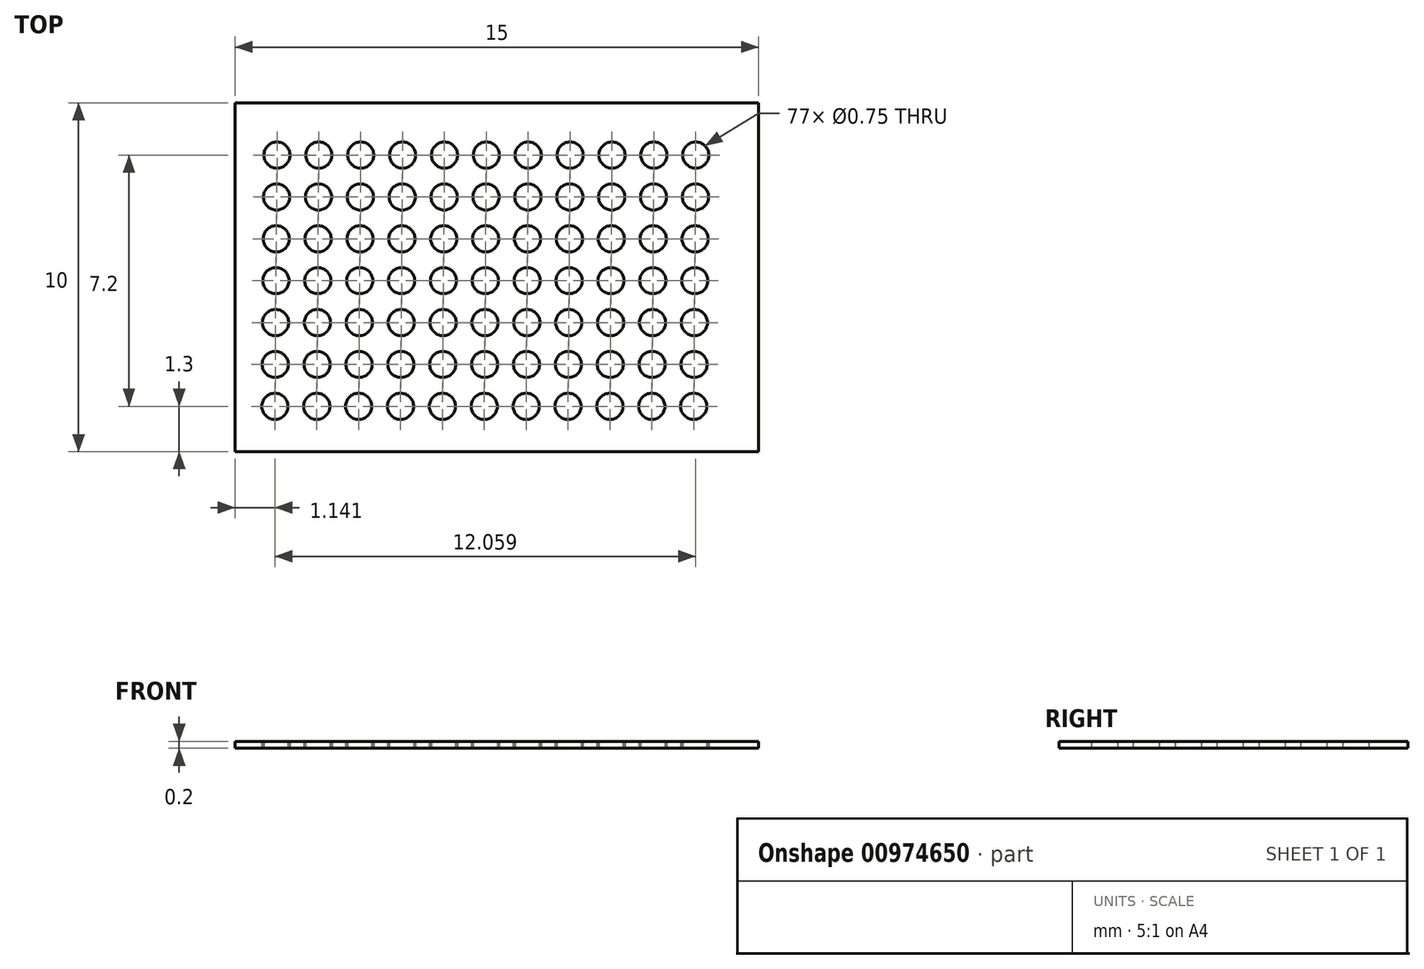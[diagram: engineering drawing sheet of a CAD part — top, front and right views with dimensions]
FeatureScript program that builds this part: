
annotation { "Feature Type Name" : "Feature", "Feature Type Description" : "" }
export const myFeature = defineFeature(function(context is Context, id is Id, definition is map)
    precondition{}
    {
        {
            var Q0;
            Q0=qCreatedBy(makeId("Top.planeOp"),FACE);
            var sketch = newSketch(context, id + "F0", { "sketchPlane" : qUnion([Q0])});
            skLineSegment(sketch, "E0.bottom", {"start": v(0, 0) * mm, "end": v(15, 0) * mm});
            skLineSegment(sketch, "E0.top", {"start": v(0, -10) * mm, "end": v(15, -10) * mm});
            skLineSegment(sketch, "E0.left", {"start": v(0, 0) * mm, "end": v(0, -10) * mm});
            skLineSegment(sketch, "E0.right", {"start": v(15, 0) * mm, "end": v(15, -10) * mm});
            skEllipse(sketch, "E1", {"center": v(1.2, -1.5) * mm, "majorRadius": 0.38 * mm, "minorRadius": 0.38 * mm, "majorAxis": v(0.93, 0.38)});
            skLineSegment(sketch, "E2.direction1", {"start": v(1.2, -1.5) * mm, "end": v(2.4, -1.5) * mm, "construction": true});
            skLineSegment(sketch, "E3.direction1", {"start": v(1.2, -1.2) * mm, "end": v(1.2, -2.1) * mm, "construction": true});
            skEllipse(sketch, "E4.0.1.0", {"center": v(2.4, -1.5) * mm, "majorRadius": 0.38 * mm, "minorRadius": 0.38 * mm, "majorAxis": v(0.93, 0.38)});
            skEllipse(sketch, "E4.0.2.0", {"center": v(3.6, -1.5) * mm, "majorRadius": 0.38 * mm, "minorRadius": 0.38 * mm, "majorAxis": v(0.93, 0.38)});
            skEllipse(sketch, "E4.0.3.0", {"center": v(4.8, -1.5) * mm, "majorRadius": 0.38 * mm, "minorRadius": 0.38 * mm, "majorAxis": v(0.93, 0.38)});
            skEllipse(sketch, "E4.0.4.0", {"center": v(6, -1.5) * mm, "majorRadius": 0.38 * mm, "minorRadius": 0.38 * mm, "majorAxis": v(0.93, 0.38)});
            skEllipse(sketch, "E4.0.5.0", {"center": v(7.2, -1.5) * mm, "majorRadius": 0.38 * mm, "minorRadius": 0.38 * mm, "majorAxis": v(0.93, 0.38)});
            skEllipse(sketch, "E4.0.6.0", {"center": v(8.4, -1.5) * mm, "majorRadius": 0.38 * mm, "minorRadius": 0.38 * mm, "majorAxis": v(0.93, 0.38)});
            skEllipse(sketch, "E4.0.7.0", {"center": v(9.6, -1.5) * mm, "majorRadius": 0.38 * mm, "minorRadius": 0.38 * mm, "majorAxis": v(0.93, 0.38)});
            skEllipse(sketch, "E4.0.8.0", {"center": v(10.8, -1.5) * mm, "majorRadius": 0.38 * mm, "minorRadius": 0.38 * mm, "majorAxis": v(0.93, 0.38)});
            skEllipse(sketch, "E4.0.9.0", {"center": v(12, -1.5) * mm, "majorRadius": 0.38 * mm, "minorRadius": 0.38 * mm, "majorAxis": v(0.93, 0.38)});
            skEllipse(sketch, "E4.0.10.0", {"center": v(13.2, -1.5) * mm, "majorRadius": 0.38 * mm, "minorRadius": 0.38 * mm, "majorAxis": v(0.93, 0.38)});
            skEllipse(sketch, "E5.1.0.0", {"center": v(2.4, -2.7) * mm, "majorRadius": 0.38 * mm, "minorRadius": 0.38 * mm, "majorAxis": v(0.93, 0.38)});
            skEllipse(sketch, "E5.1.0.1", {"center": v(1.2, -2.7) * mm, "majorRadius": 0.38 * mm, "minorRadius": 0.38 * mm, "majorAxis": v(0.93, 0.38)});
            skEllipse(sketch, "E5.1.0.2", {"center": v(6, -2.7) * mm, "majorRadius": 0.38 * mm, "minorRadius": 0.38 * mm, "majorAxis": v(0.93, 0.38)});
            skLineSegment(sketch, "E5.1.0.3", {"start": v(1.2, -2.7) * mm, "end": v(2.4, -2.7) * mm, "construction": true});
            skEllipse(sketch, "E5.1.0.4", {"center": v(3.6, -2.7) * mm, "majorRadius": 0.38 * mm, "minorRadius": 0.38 * mm, "majorAxis": v(0.93, 0.38)});
            skEllipse(sketch, "E5.1.0.5", {"center": v(8.4, -2.7) * mm, "majorRadius": 0.38 * mm, "minorRadius": 0.38 * mm, "majorAxis": v(0.93, 0.38)});
            skEllipse(sketch, "E5.1.0.6", {"center": v(9.6, -2.7) * mm, "majorRadius": 0.38 * mm, "minorRadius": 0.38 * mm, "majorAxis": v(0.93, 0.38)});
            skEllipse(sketch, "E5.1.0.7", {"center": v(7.2, -2.7) * mm, "majorRadius": 0.38 * mm, "minorRadius": 0.38 * mm, "majorAxis": v(0.93, 0.38)});
            skEllipse(sketch, "E5.1.0.8", {"center": v(13.2, -2.7) * mm, "majorRadius": 0.38 * mm, "minorRadius": 0.38 * mm, "majorAxis": v(0.93, 0.38)});
            skEllipse(sketch, "E5.1.0.9", {"center": v(4.8, -2.7) * mm, "majorRadius": 0.38 * mm, "minorRadius": 0.38 * mm, "majorAxis": v(0.93, 0.38)});
            skEllipse(sketch, "E5.1.0.10", {"center": v(12, -2.7) * mm, "majorRadius": 0.38 * mm, "minorRadius": 0.38 * mm, "majorAxis": v(0.93, 0.38)});
            skEllipse(sketch, "E5.1.0.11", {"center": v(10.8, -2.7) * mm, "majorRadius": 0.38 * mm, "minorRadius": 0.38 * mm, "majorAxis": v(0.93, 0.38)});
            skLineSegment(sketch, "E5.1.0.12", {"start": v(1.2, -2.4) * mm, "end": v(1.2, -3.3) * mm, "construction": true});
            skEllipse(sketch, "E5.2.0.0", {"center": v(2.38, -3.9) * mm, "majorRadius": 0.38 * mm, "minorRadius": 0.38 * mm, "majorAxis": v(0.93, 0.38)});
            skEllipse(sketch, "E5.2.0.1", {"center": v(1.18, -3.9) * mm, "majorRadius": 0.38 * mm, "minorRadius": 0.38 * mm, "majorAxis": v(0.93, 0.38)});
            skEllipse(sketch, "E5.2.0.2", {"center": v(5.98, -3.9) * mm, "majorRadius": 0.38 * mm, "minorRadius": 0.38 * mm, "majorAxis": v(0.93, 0.38)});
            skLineSegment(sketch, "E5.2.0.3", {"start": v(1.18, -3.9) * mm, "end": v(2.38, -3.9) * mm, "construction": true});
            skEllipse(sketch, "E5.2.0.4", {"center": v(3.58, -3.9) * mm, "majorRadius": 0.38 * mm, "minorRadius": 0.38 * mm, "majorAxis": v(0.93, 0.38)});
            skEllipse(sketch, "E5.2.0.5", {"center": v(8.38, -3.9) * mm, "majorRadius": 0.38 * mm, "minorRadius": 0.38 * mm, "majorAxis": v(0.93, 0.38)});
            skEllipse(sketch, "E5.2.0.6", {"center": v(9.58, -3.9) * mm, "majorRadius": 0.38 * mm, "minorRadius": 0.38 * mm, "majorAxis": v(0.93, 0.38)});
            skEllipse(sketch, "E5.2.0.7", {"center": v(7.18, -3.9) * mm, "majorRadius": 0.38 * mm, "minorRadius": 0.38 * mm, "majorAxis": v(0.93, 0.38)});
            skEllipse(sketch, "E5.2.0.8", {"center": v(13.18, -3.9) * mm, "majorRadius": 0.38 * mm, "minorRadius": 0.38 * mm, "majorAxis": v(0.93, 0.38)});
            skEllipse(sketch, "E5.2.0.9", {"center": v(4.78, -3.9) * mm, "majorRadius": 0.38 * mm, "minorRadius": 0.38 * mm, "majorAxis": v(0.93, 0.38)});
            skEllipse(sketch, "E5.2.0.10", {"center": v(11.98, -3.9) * mm, "majorRadius": 0.38 * mm, "minorRadius": 0.38 * mm, "majorAxis": v(0.93, 0.38)});
            skEllipse(sketch, "E5.2.0.11", {"center": v(10.78, -3.9) * mm, "majorRadius": 0.38 * mm, "minorRadius": 0.38 * mm, "majorAxis": v(0.93, 0.38)});
            skLineSegment(sketch, "E5.2.0.12", {"start": v(1.18, -3.6) * mm, "end": v(1.18, -4.5) * mm, "construction": true});
            skEllipse(sketch, "E5.3.0.0", {"center": v(2.37, -5.1) * mm, "majorRadius": 0.38 * mm, "minorRadius": 0.38 * mm, "majorAxis": v(0.93, 0.38)});
            skEllipse(sketch, "E5.3.0.1", {"center": v(1.17, -5.1) * mm, "majorRadius": 0.38 * mm, "minorRadius": 0.38 * mm, "majorAxis": v(0.93, 0.38)});
            skEllipse(sketch, "E5.3.0.2", {"center": v(5.97, -5.1) * mm, "majorRadius": 0.38 * mm, "minorRadius": 0.38 * mm, "majorAxis": v(0.93, 0.38)});
            skLineSegment(sketch, "E5.3.0.3", {"start": v(1.17, -5.1) * mm, "end": v(2.37, -5.1) * mm, "construction": true});
            skEllipse(sketch, "E5.3.0.4", {"center": v(3.57, -5.1) * mm, "majorRadius": 0.38 * mm, "minorRadius": 0.38 * mm, "majorAxis": v(0.93, 0.38)});
            skEllipse(sketch, "E5.3.0.5", {"center": v(8.37, -5.1) * mm, "majorRadius": 0.38 * mm, "minorRadius": 0.38 * mm, "majorAxis": v(0.93, 0.38)});
            skEllipse(sketch, "E5.3.0.6", {"center": v(9.57, -5.1) * mm, "majorRadius": 0.38 * mm, "minorRadius": 0.38 * mm, "majorAxis": v(0.93, 0.38)});
            skEllipse(sketch, "E5.3.0.7", {"center": v(7.17, -5.1) * mm, "majorRadius": 0.38 * mm, "minorRadius": 0.38 * mm, "majorAxis": v(0.93, 0.38)});
            skEllipse(sketch, "E5.3.0.8", {"center": v(13.17, -5.1) * mm, "majorRadius": 0.38 * mm, "minorRadius": 0.38 * mm, "majorAxis": v(0.93, 0.38)});
            skEllipse(sketch, "E5.3.0.9", {"center": v(4.77, -5.1) * mm, "majorRadius": 0.38 * mm, "minorRadius": 0.38 * mm, "majorAxis": v(0.93, 0.38)});
            skEllipse(sketch, "E5.3.0.10", {"center": v(11.97, -5.1) * mm, "majorRadius": 0.38 * mm, "minorRadius": 0.38 * mm, "majorAxis": v(0.93, 0.38)});
            skEllipse(sketch, "E5.3.0.11", {"center": v(10.77, -5.1) * mm, "majorRadius": 0.38 * mm, "minorRadius": 0.38 * mm, "majorAxis": v(0.93, 0.38)});
            skLineSegment(sketch, "E5.3.0.12", {"start": v(1.17, -4.8) * mm, "end": v(1.17, -5.7) * mm, "construction": true});
            skEllipse(sketch, "E5.4.0.0", {"center": v(2.36, -6.3) * mm, "majorRadius": 0.38 * mm, "minorRadius": 0.38 * mm, "majorAxis": v(0.93, 0.38)});
            skEllipse(sketch, "E5.4.0.1", {"center": v(1.16, -6.3) * mm, "majorRadius": 0.38 * mm, "minorRadius": 0.38 * mm, "majorAxis": v(0.93, 0.38)});
            skEllipse(sketch, "E5.4.0.2", {"center": v(5.96, -6.3) * mm, "majorRadius": 0.38 * mm, "minorRadius": 0.38 * mm, "majorAxis": v(0.93, 0.38)});
            skLineSegment(sketch, "E5.4.0.3", {"start": v(1.16, -6.3) * mm, "end": v(2.36, -6.3) * mm, "construction": true});
            skEllipse(sketch, "E5.4.0.4", {"center": v(3.56, -6.3) * mm, "majorRadius": 0.38 * mm, "minorRadius": 0.38 * mm, "majorAxis": v(0.93, 0.38)});
            skEllipse(sketch, "E5.4.0.5", {"center": v(8.36, -6.3) * mm, "majorRadius": 0.38 * mm, "minorRadius": 0.38 * mm, "majorAxis": v(0.93, 0.38)});
            skEllipse(sketch, "E5.4.0.6", {"center": v(9.56, -6.3) * mm, "majorRadius": 0.38 * mm, "minorRadius": 0.38 * mm, "majorAxis": v(0.93, 0.38)});
            skEllipse(sketch, "E5.4.0.7", {"center": v(7.16, -6.3) * mm, "majorRadius": 0.38 * mm, "minorRadius": 0.38 * mm, "majorAxis": v(0.93, 0.38)});
            skEllipse(sketch, "E5.4.0.8", {"center": v(13.16, -6.3) * mm, "majorRadius": 0.38 * mm, "minorRadius": 0.38 * mm, "majorAxis": v(0.93, 0.38)});
            skEllipse(sketch, "E5.4.0.9", {"center": v(4.76, -6.3) * mm, "majorRadius": 0.38 * mm, "minorRadius": 0.38 * mm, "majorAxis": v(0.93, 0.38)});
            skEllipse(sketch, "E5.4.0.10", {"center": v(11.96, -6.3) * mm, "majorRadius": 0.38 * mm, "minorRadius": 0.38 * mm, "majorAxis": v(0.93, 0.38)});
            skEllipse(sketch, "E5.4.0.11", {"center": v(10.76, -6.3) * mm, "majorRadius": 0.38 * mm, "minorRadius": 0.38 * mm, "majorAxis": v(0.93, 0.38)});
            skLineSegment(sketch, "E5.4.0.12", {"start": v(1.16, -6) * mm, "end": v(1.16, -6.9) * mm, "construction": true});
            skEllipse(sketch, "E5.5.0.0", {"center": v(2.35, -7.5) * mm, "majorRadius": 0.38 * mm, "minorRadius": 0.38 * mm, "majorAxis": v(0.93, 0.38)});
            skEllipse(sketch, "E5.5.0.1", {"center": v(1.15, -7.5) * mm, "majorRadius": 0.38 * mm, "minorRadius": 0.38 * mm, "majorAxis": v(0.93, 0.38)});
            skEllipse(sketch, "E5.5.0.2", {"center": v(5.95, -7.5) * mm, "majorRadius": 0.38 * mm, "minorRadius": 0.38 * mm, "majorAxis": v(0.93, 0.38)});
            skLineSegment(sketch, "E5.5.0.3", {"start": v(1.15, -7.5) * mm, "end": v(2.35, -7.5) * mm, "construction": true});
            skEllipse(sketch, "E5.5.0.4", {"center": v(3.55, -7.5) * mm, "majorRadius": 0.38 * mm, "minorRadius": 0.38 * mm, "majorAxis": v(0.93, 0.38)});
            skEllipse(sketch, "E5.5.0.5", {"center": v(8.35, -7.5) * mm, "majorRadius": 0.38 * mm, "minorRadius": 0.38 * mm, "majorAxis": v(0.93, 0.38)});
            skEllipse(sketch, "E5.5.0.6", {"center": v(9.55, -7.5) * mm, "majorRadius": 0.38 * mm, "minorRadius": 0.38 * mm, "majorAxis": v(0.93, 0.38)});
            skEllipse(sketch, "E5.5.0.7", {"center": v(7.15, -7.5) * mm, "majorRadius": 0.38 * mm, "minorRadius": 0.38 * mm, "majorAxis": v(0.93, 0.38)});
            skEllipse(sketch, "E5.5.0.8", {"center": v(13.15, -7.5) * mm, "majorRadius": 0.38 * mm, "minorRadius": 0.38 * mm, "majorAxis": v(0.93, 0.38)});
            skEllipse(sketch, "E5.5.0.9", {"center": v(4.75, -7.5) * mm, "majorRadius": 0.38 * mm, "minorRadius": 0.38 * mm, "majorAxis": v(0.93, 0.38)});
            skEllipse(sketch, "E5.5.0.10", {"center": v(11.95, -7.5) * mm, "majorRadius": 0.38 * mm, "minorRadius": 0.38 * mm, "majorAxis": v(0.93, 0.38)});
            skEllipse(sketch, "E5.5.0.11", {"center": v(10.75, -7.5) * mm, "majorRadius": 0.38 * mm, "minorRadius": 0.38 * mm, "majorAxis": v(0.93, 0.38)});
            skLineSegment(sketch, "E5.5.0.12", {"start": v(1.15, -7.2) * mm, "end": v(1.15, -8.1) * mm, "construction": true});
            skEllipse(sketch, "E5.6.0.0", {"center": v(2.34, -8.7) * mm, "majorRadius": 0.38 * mm, "minorRadius": 0.38 * mm, "majorAxis": v(0.93, 0.38)});
            skEllipse(sketch, "E5.6.0.1", {"center": v(1.14, -8.7) * mm, "majorRadius": 0.38 * mm, "minorRadius": 0.38 * mm, "majorAxis": v(0.93, 0.38)});
            skEllipse(sketch, "E5.6.0.2", {"center": v(5.94, -8.7) * mm, "majorRadius": 0.38 * mm, "minorRadius": 0.38 * mm, "majorAxis": v(0.93, 0.38)});
            skLineSegment(sketch, "E5.6.0.3", {"start": v(1.14, -8.7) * mm, "end": v(2.34, -8.7) * mm, "construction": true});
            skEllipse(sketch, "E5.6.0.4", {"center": v(3.54, -8.7) * mm, "majorRadius": 0.38 * mm, "minorRadius": 0.38 * mm, "majorAxis": v(0.93, 0.38)});
            skEllipse(sketch, "E5.6.0.5", {"center": v(8.34, -8.7) * mm, "majorRadius": 0.38 * mm, "minorRadius": 0.38 * mm, "majorAxis": v(0.93, 0.38)});
            skEllipse(sketch, "E5.6.0.6", {"center": v(9.54, -8.7) * mm, "majorRadius": 0.38 * mm, "minorRadius": 0.38 * mm, "majorAxis": v(0.93, 0.38)});
            skEllipse(sketch, "E5.6.0.7", {"center": v(7.14, -8.7) * mm, "majorRadius": 0.38 * mm, "minorRadius": 0.38 * mm, "majorAxis": v(0.93, 0.38)});
            skEllipse(sketch, "E5.6.0.8", {"center": v(13.14, -8.7) * mm, "majorRadius": 0.38 * mm, "minorRadius": 0.38 * mm, "majorAxis": v(0.93, 0.38)});
            skEllipse(sketch, "E5.6.0.9", {"center": v(4.74, -8.7) * mm, "majorRadius": 0.38 * mm, "minorRadius": 0.38 * mm, "majorAxis": v(0.93, 0.38)});
            skEllipse(sketch, "E5.6.0.10", {"center": v(11.94, -8.7) * mm, "majorRadius": 0.38 * mm, "minorRadius": 0.38 * mm, "majorAxis": v(0.93, 0.38)});
            skEllipse(sketch, "E5.6.0.11", {"center": v(10.74, -8.7) * mm, "majorRadius": 0.38 * mm, "minorRadius": 0.38 * mm, "majorAxis": v(0.93, 0.38)});
            skLineSegment(sketch, "E5.6.0.12", {"start": v(1.14, -8.4) * mm, "end": v(1.14, -9.3) * mm, "construction": true});
            skLineSegment(sketch, "E5.direction1", {"start": v(1.2, -2.1) * mm, "end": v(1.2, -3.3) * mm, "construction": true});
            skSolve(sketch);
        }
        {
            var Q0;
            Q0=makeQuery(id+"F0.imprint","IMPRINT",FACE,{"disambiguationData":[TD([[makeQuery(id+"F0.imprint","IMPRINT",EDGE,{"derivedFrom":sQuery(id+"F0.wireOp",EDGE,"E0.bottom")}),-1.0]])]});
            extrude(context, id + "F1", {"entities" : qUnion([Q0]), "depth" : 0.2 * mm, "offsetDistance" : 25.4 * mm});
        }
    });
